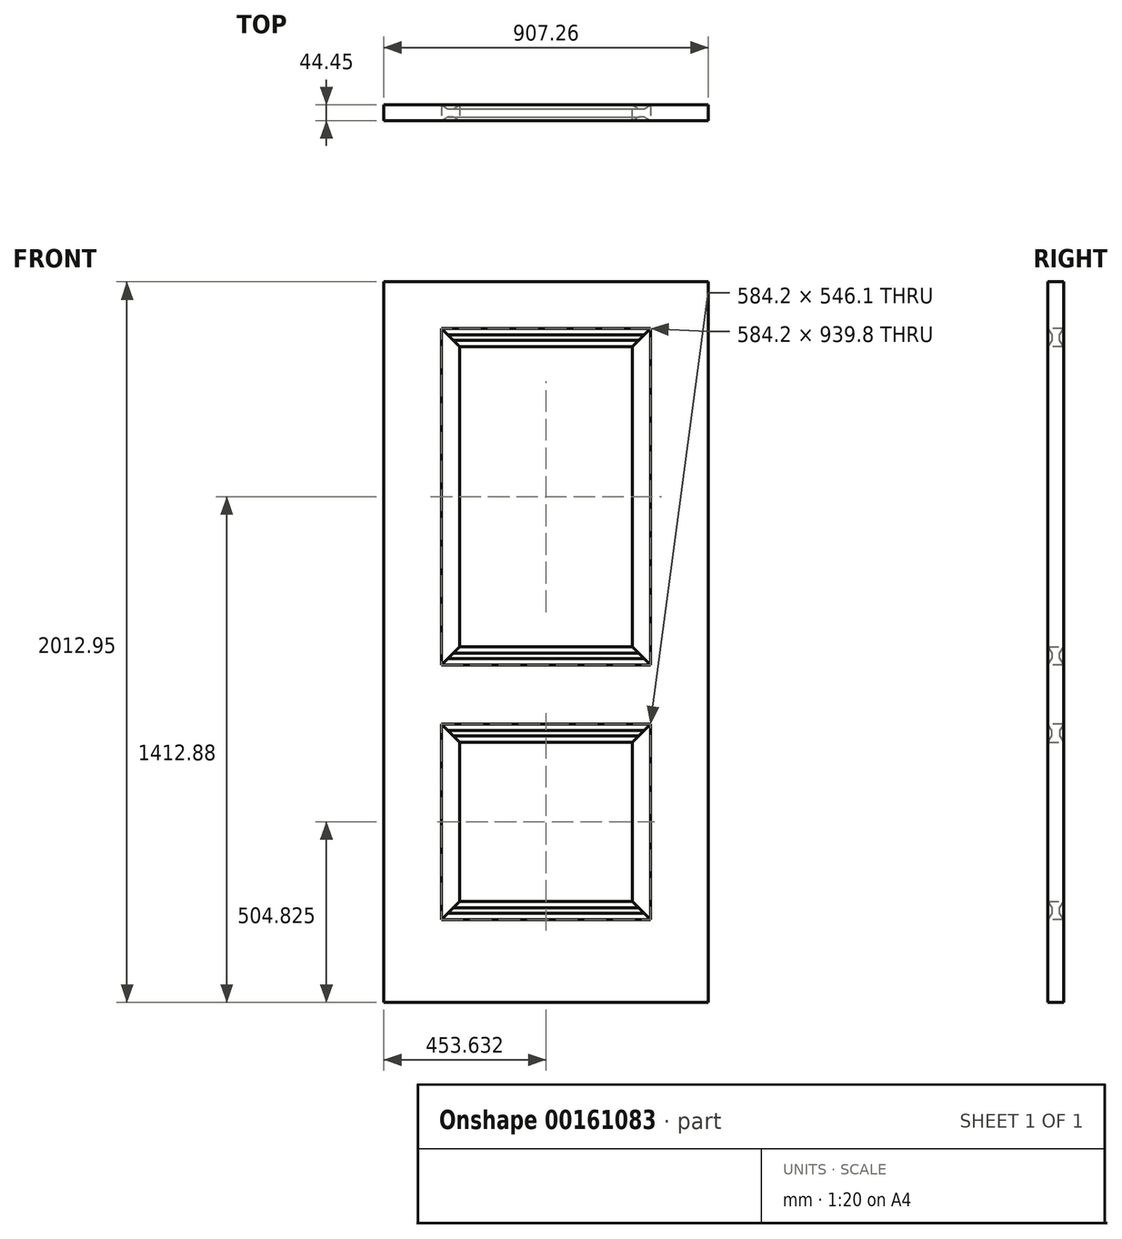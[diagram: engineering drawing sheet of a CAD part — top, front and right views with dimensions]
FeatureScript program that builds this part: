
annotation { "Feature Type Name" : "Feature", "Feature Type Description" : "" }
export const myFeature = defineFeature(function(context is Context, id is Id, definition is map)
    precondition{}
    {
        {
            var Q0;
            Q0=qCreatedBy(makeId("Top.planeOp"),FACE);
            var sketch = newSketch(context, id + "F0", { "sketchPlane" : qUnion([Q0])});
            skLineSegment(sketch, "E0.bottom", {"start": v(0, 0) * mm, "end": v(-907.26, 0) * mm});
            skLineSegment(sketch, "E0.top", {"start": v(0, 44.45) * mm, "end": v(-907.26, 44.45) * mm});
            skLineSegment(sketch, "E0.left", {"start": v(0, 0) * mm, "end": v(0, 44.45) * mm});
            skLineSegment(sketch, "E0.right", {"start": v(-907.26, 0) * mm, "end": v(-907.26, 44.45) * mm});
            skSolve(sketch);
        }
        {
            var Q0;
            Q0=qSketchRegion(id+"F0",true);
            extrude(context, id + "F1", {"entities" : qUnion([Q0]), "depth" : 2012.95 * mm});
        }
        {
            var Q0;
            Q0=qCreatedBy(makeId("Front.planeOp"),FACE);
            var sketch = newSketch(context, id + "F2", { "sketchPlane" : qUnion([Q0])});
            skLineSegment(sketch, "E1.top", {"start": v(-745.73, 942.97) * mm, "end": v(-161.53, 942.98) * mm});
            skLineSegment(sketch, "E1.left", {"start": v(-745.73, 1882.78) * mm, "end": v(-745.73, 942.97) * mm});
            skLineSegment(sketch, "E1.right", {"start": v(-161.53, 1882.78) * mm, "end": v(-161.53, 942.98) * mm});
            skLineSegment(sketch, "E2", {"start": v(-745.73, 1882.78) * mm, "end": v(-453.63, 1882.78) * mm});
            skLineSegment(sketch, "E3", {"start": v(-453.63, 1882.78) * mm, "end": v(-161.53, 1882.78) * mm});
            skPoint(sketch, "E4.0", {"position": v(-453.63, 2012.95) * mm});
            skLineSegment(sketch, "E5.bottom", {"start": v(-745.73, 777.88) * mm, "end": v(-161.53, 777.88) * mm});
            skLineSegment(sketch, "E5.top", {"start": v(-745.73, 231.78) * mm, "end": v(-161.53, 231.78) * mm});
            skLineSegment(sketch, "E5.left", {"start": v(-745.73, 777.88) * mm, "end": v(-745.73, 231.78) * mm});
            skLineSegment(sketch, "E5.right", {"start": v(-161.53, 777.88) * mm, "end": v(-161.53, 231.78) * mm});
            skSolve(sketch);
        }
        {
            var Q0;
            Q0 = qSketchRegion(id + "F2", true);
            extrude(context, id + "F3", {"entities" : qUnion([Q0]), "operationType" : NewBodyOperationType.REMOVE, "endBound" : BoundingType.THROUGH_ALL, "oppositeDirection" : true, "depth" : 25.4 * mm});
        }
        {
            var Q0;
            Q0=qCreatedBy(makeId("Top.planeOp"),FACE);
            var sketch = newSketch(context, id + "F4", { "sketchPlane" : qUnion([Q0])});
            skPoint(sketch, "E6.0", {"position": v(-161.53, 22.23) * mm});
            skPoint(sketch, "E7.0", {"position": v(-161.53, 44.45) * mm});
            skLineSegment(sketch, "E8", {"start": v(-161.53, 22.23) * mm, "end": v(-161.53, 44.45) * mm});
            skLineSegment(sketch, "E9", {"start": v(-161.53, 44.45) * mm, "end": v(-179, 33.62) * mm});
            skLineSegment(sketch, "E10", {"start": v(-179, 33.62) * mm, "end": v(-186.93, 33.62) * mm});
            skLineSegment(sketch, "E11", {"start": v(-186.93, 33.62) * mm, "end": v(-186.93, 59.2) * mm, "construction": true});
            skLineSegment(sketch, "E12", {"start": v(-161.53, 22.23) * mm, "end": v(-138.76, 22.23) * mm, "construction": true});
            skLineSegment(sketch, "E13.MirrorCS", {"start": v(-194.86, 33.62) * mm, "end": v(-186.93, 33.62) * mm});
            skLineSegment(sketch, "E14.MirrorCS", {"start": v(-212.33, 44.45) * mm, "end": v(-194.86, 33.62) * mm});
            skLineSegment(sketch, "E15.MirrorCS", {"start": v(-212.33, 22.23) * mm, "end": v(-212.33, 44.45) * mm});
            skLineSegment(sketch, "E16.MirrorCS", {"start": v(-161.53, 22.23) * mm, "end": v(-161.53, 0) * mm});
            skLineSegment(sketch, "E17.MirrorCS", {"start": v(-161.53, 0) * mm, "end": v(-179, 10.83) * mm});
            skLineSegment(sketch, "E18.MirrorCS", {"start": v(-179, 10.83) * mm, "end": v(-186.93, 10.83) * mm});
            skLineSegment(sketch, "E19.MirrorCS", {"start": v(-194.86, 10.83) * mm, "end": v(-186.93, 10.83) * mm});
            skLineSegment(sketch, "E20.MirrorCS", {"start": v(-212.33, 0) * mm, "end": v(-194.86, 10.83) * mm});
            skLineSegment(sketch, "E21.MirrorCS", {"start": v(-212.33, 22.23) * mm, "end": v(-212.33, 0) * mm});
            skPoint(sketch, "E22.0", {"position": v(-745.73, 22.23) * mm});
            skLineSegment(sketch, "E23", {"start": v(-161.53, 126.67) * mm, "end": v(-745.73, 126.67) * mm, "construction": true});
            skLineSegment(sketch, "E24", {"start": v(-453.63, 126.67) * mm, "end": v(-453.63, 173.15) * mm, "construction": true});
            skPoint(sketch, "E24.endSnap0", {"position": v(-453.63, 126.67) * mm});
            skLineSegment(sketch, "E25.MirrorCS", {"start": v(-712.4, 10.83) * mm, "end": v(-720.33, 10.83) * mm});
            skLineSegment(sketch, "E26.MirrorCS", {"start": v(-712.4, 33.62) * mm, "end": v(-720.33, 33.62) * mm});
            skLineSegment(sketch, "E27.MirrorCS", {"start": v(-728.26, 10.83) * mm, "end": v(-720.33, 10.83) * mm});
            skLineSegment(sketch, "E28.MirrorCS", {"start": v(-728.26, 33.62) * mm, "end": v(-720.33, 33.62) * mm});
            skLineSegment(sketch, "E29.MirrorCS", {"start": v(-694.93, 0) * mm, "end": v(-712.4, 10.83) * mm});
            skLineSegment(sketch, "E30.MirrorCS", {"start": v(-694.93, 44.45) * mm, "end": v(-712.4, 33.62) * mm});
            skLineSegment(sketch, "E31.MirrorCS", {"start": v(-745.73, 0) * mm, "end": v(-728.26, 10.83) * mm});
            skLineSegment(sketch, "E32.MirrorCS", {"start": v(-745.73, 22.23) * mm, "end": v(-745.73, 44.45) * mm});
            skLineSegment(sketch, "E33.MirrorCS", {"start": v(-694.93, 22.23) * mm, "end": v(-694.93, 0) * mm});
            skPoint(sketch, "E34.MirrorP", {"position": v(-745.73, 44.45) * mm});
            skLineSegment(sketch, "E35.MirrorCS", {"start": v(-745.73, 22.23) * mm, "end": v(-745.73, 0) * mm});
            skLineSegment(sketch, "E36.MirrorCS", {"start": v(-745.73, 44.45) * mm, "end": v(-728.26, 33.62) * mm});
            skLineSegment(sketch, "E37.MirrorCS", {"start": v(-694.93, 22.23) * mm, "end": v(-694.93, 44.45) * mm});
            skSolve(sketch);
        }
        {
            var Q0;
            Q0=qCreatedBy(makeId("Front.planeOp"),FACE);
            var sketch = newSketch(context, id + "F5", { "sketchPlane" : qUnion([Q0])});
            skPoint(sketch, "E38.0", {"position": v(-745.73, 1882.78) * mm});
            skPoint(sketch, "E39.0", {"position": v(-161.53, 1882.78) * mm});
            skPoint(sketch, "E40.0", {"position": v(-161.53, 942.97) * mm});
            skPoint(sketch, "E41.0", {"position": v(-745.73, 942.97) * mm});
            skPoint(sketch, "E42.0", {"position": v(-745.73, 777.88) * mm});
            skPoint(sketch, "E43.0", {"position": v(-161.53, 777.88) * mm});
            skPoint(sketch, "E44.0", {"position": v(-745.73, 231.78) * mm});
            skPoint(sketch, "E45.0", {"position": v(-161.53, 231.78) * mm});
            skLineSegment(sketch, "E46", {"start": v(-745.73, 1882.78) * mm, "end": v(-453.63, 1590.68) * mm});
            skLineSegment(sketch, "E47", {"start": v(-453.63, 1590.68) * mm, "end": v(-161.53, 1882.78) * mm});
            skLineSegment(sketch, "E48", {"start": v(-745.73, 777.88) * mm, "end": v(-453.63, 485.78) * mm});
            skLineSegment(sketch, "E49", {"start": v(-453.63, 485.77) * mm, "end": v(-161.53, 777.88) * mm});
            skLineSegment(sketch, "E50", {"start": v(-745.73, 1882.78) * mm, "end": v(-875.9, 2012.95) * mm});
            skLineSegment(sketch, "E51", {"start": v(-875.9, 2012.95) * mm, "end": v(-31.35, 2012.95) * mm});
            skLineSegment(sketch, "E52", {"start": v(-31.35, 2012.95) * mm, "end": v(-161.53, 1882.78) * mm});
            skLineSegment(sketch, "E53", {"start": v(-745.73, 777.88) * mm, "end": v(-1980.8, 2012.95) * mm});
            skLineSegment(sketch, "E54", {"start": v(-1980.8, 2012.95) * mm, "end": v(1073.55, 2012.95) * mm});
            skLineSegment(sketch, "E55", {"start": v(1073.55, 2012.95) * mm, "end": v(-161.53, 777.88) * mm});
            skLineSegment(sketch, "E56", {"start": v(-745.73, 942.97) * mm, "end": v(-453.63, 1235.07) * mm});
            skLineSegment(sketch, "E57", {"start": v(-453.63, 1235.07) * mm, "end": v(-161.53, 942.97) * mm});
            skLineSegment(sketch, "E58", {"start": v(-745.73, 231.77) * mm, "end": v(-453.63, 523.88) * mm});
            skLineSegment(sketch, "E59", {"start": v(-453.63, 523.88) * mm, "end": v(-161.53, 231.78) * mm});
            skLineSegment(sketch, "E60", {"start": v(-745.73, 942.97) * mm, "end": v(-1688.7, 0) * mm});
            skLineSegment(sketch, "E61", {"start": v(-1688.7, 0) * mm, "end": v(781.45, 0) * mm});
            skLineSegment(sketch, "E62", {"start": v(781.45, 0) * mm, "end": v(-161.53, 942.98) * mm});
            skLineSegment(sketch, "E63", {"start": v(-161.53, 231.78) * mm, "end": v(70.25, 0) * mm});
            skLineSegment(sketch, "E64", {"start": v(70.25, 0) * mm, "end": v(-977.5, 0) * mm});
            skLineSegment(sketch, "E65", {"start": v(-977.5, 0) * mm, "end": v(-745.73, 231.78) * mm});
            skSolve(sketch);
        }
        {
            var Q0;
            Q0=makeQuery(id+"F3.boolean.opBoolean","COPY",FACE,{"derivedFrom":makeQuery(id+"F3.opExtrude","SWEPT_FACE",FACE,{"disambiguationData":[OSD([sQuery(id+"F2.wireOp",EDGE,"E2"),sQuery(id+"F2.wireOp",EDGE,"E3")])]})});
            var sketch = newSketch(context, id + "F6", { "sketchPlane" : qUnion([Q0])});
            skLineSegment(sketch, "E66.2", {"start": v(-694.93, 0) * mm, "end": v(-712.4, -10.83) * mm});
            skLineSegment(sketch, "E66.4", {"start": v(-212.33, -44.45) * mm, "end": v(-194.86, -33.62) * mm});
            skLineSegment(sketch, "E66.5", {"start": v(-694.93, -22.23) * mm, "end": v(-694.93, 0) * mm});
            skLineSegment(sketch, "E66.6", {"start": v(-212.33, -22.23) * mm, "end": v(-212.33, -44.45) * mm});
            skLineSegment(sketch, "E66.7", {"start": v(-694.93, -44.45) * mm, "end": v(-712.4, -33.62) * mm});
            skLineSegment(sketch, "E66.8", {"start": v(-212.33, 0) * mm, "end": v(-194.86, -10.83) * mm});
            skLineSegment(sketch, "E66.9", {"start": v(-212.33, -22.23) * mm, "end": v(-212.33, 0) * mm});
            skLineSegment(sketch, "E66.10", {"start": v(-694.93, -22.23) * mm, "end": v(-694.93, -44.45) * mm});
            skLineSegment(sketch, "E66.11", {"start": v(-161.53, -44.45) * mm, "end": v(-179, -33.62) * mm});
            skLineSegment(sketch, "E66.12", {"start": v(-712.4, -33.62) * mm, "end": v(-720.33, -33.62) * mm});
            skLineSegment(sketch, "E66.14", {"start": v(-194.86, -33.62) * mm, "end": v(-186.93, -33.62) * mm});
            skLineSegment(sketch, "E66.15", {"start": v(-745.73, -44.45) * mm, "end": v(-728.26, -33.62) * mm});
            skLineSegment(sketch, "E66.16", {"start": v(-161.53, -22.23) * mm, "end": v(-161.53, 0) * mm});
            skLineSegment(sketch, "E66.17", {"start": v(-161.53, 0) * mm, "end": v(-179, -10.83) * mm});
            skLineSegment(sketch, "E66.18", {"start": v(-179, -10.83) * mm, "end": v(-186.93, -10.83) * mm});
            skLineSegment(sketch, "E66.19", {"start": v(-194.86, -10.83) * mm, "end": v(-186.93, -10.83) * mm});
            skLineSegment(sketch, "E66.20", {"start": v(-745.73, 0) * mm, "end": v(-728.26, -10.83) * mm});
            skLineSegment(sketch, "E66.21", {"start": v(-745.73, -22.23) * mm, "end": v(-745.73, -44.45) * mm});
            skLineSegment(sketch, "E66.22", {"start": v(-728.26, -10.83) * mm, "end": v(-720.33, -10.83) * mm});
            skLineSegment(sketch, "E66.23", {"start": v(-745.73, -22.23) * mm, "end": v(-745.73, 0) * mm});
            skLineSegment(sketch, "E66.24", {"start": v(-712.4, -10.83) * mm, "end": v(-720.33, -10.83) * mm});
            skLineSegment(sketch, "E66.25", {"start": v(-161.53, -22.23) * mm, "end": v(-161.53, -44.45) * mm});
            skLineSegment(sketch, "E66.26", {"start": v(-179, -33.62) * mm, "end": v(-186.93, -33.62) * mm});
            skLineSegment(sketch, "E66.27", {"start": v(-728.26, -33.62) * mm, "end": v(-720.33, -33.62) * mm});
            skSolve(sketch);
        }
        {
            var Q0;
            Q0=makeQuery(id+"F3.boolean.opBoolean","COPY",FACE,{"derivedFrom":makeQuery(id+"F3.opExtrude","SWEPT_FACE",FACE,{"disambiguationData":[OSD([sQuery(id+"F2.wireOp",EDGE,"E5.top")])]})});
            var sketch = newSketch(context, id + "F7", { "sketchPlane" : qUnion([Q0])});
            skLineSegment(sketch, "E67.0", {"start": v(-745.73, 0) * mm, "end": v(-728.26, 10.83) * mm});
            skLineSegment(sketch, "E67.1", {"start": v(-694.93, 0) * mm, "end": v(-712.4, 10.83) * mm});
            skLineSegment(sketch, "E67.2", {"start": v(-745.73, 22.23) * mm, "end": v(-745.73, 44.45) * mm});
            skLineSegment(sketch, "E67.3", {"start": v(-728.26, 10.83) * mm, "end": v(-720.33, 10.83) * mm});
            skLineSegment(sketch, "E67.4", {"start": v(-745.73, 22.23) * mm, "end": v(-745.73, 0) * mm});
            skLineSegment(sketch, "E67.5", {"start": v(-694.93, 22.23) * mm, "end": v(-694.93, 44.45) * mm});
            skLineSegment(sketch, "E67.6", {"start": v(-712.4, 10.83) * mm, "end": v(-720.33, 10.83) * mm});
            skLineSegment(sketch, "E67.7", {"start": v(-712.4, 33.62) * mm, "end": v(-720.33, 33.62) * mm});
            skLineSegment(sketch, "E67.8", {"start": v(-745.73, 44.45) * mm, "end": v(-728.26, 33.62) * mm});
            skLineSegment(sketch, "E67.9", {"start": v(-694.93, 22.23) * mm, "end": v(-694.93, 0) * mm});
            skLineSegment(sketch, "E67.10", {"start": v(-694.93, 44.45) * mm, "end": v(-712.4, 33.62) * mm});
            skLineSegment(sketch, "E67.11", {"start": v(-728.26, 33.62) * mm, "end": v(-720.33, 33.62) * mm});
            skLineSegment(sketch, "E68.0", {"start": v(-212.33, 22.23) * mm, "end": v(-212.33, 0) * mm});
            skLineSegment(sketch, "E68.1", {"start": v(-161.53, 22.23) * mm, "end": v(-161.53, 44.45) * mm});
            skLineSegment(sketch, "E68.2", {"start": v(-161.53, 44.45) * mm, "end": v(-179, 33.62) * mm});
            skLineSegment(sketch, "E68.3", {"start": v(-179, 33.62) * mm, "end": v(-186.93, 33.62) * mm});
            skLineSegment(sketch, "E68.4", {"start": v(-194.86, 33.62) * mm, "end": v(-186.93, 33.62) * mm});
            skLineSegment(sketch, "E68.5", {"start": v(-212.33, 44.45) * mm, "end": v(-194.86, 33.62) * mm});
            skLineSegment(sketch, "E68.6", {"start": v(-212.33, 22.23) * mm, "end": v(-212.33, 44.45) * mm});
            skLineSegment(sketch, "E68.7", {"start": v(-161.53, 22.23) * mm, "end": v(-161.53, 0) * mm});
            skLineSegment(sketch, "E68.8", {"start": v(-161.53, 0) * mm, "end": v(-179, 10.83) * mm});
            skLineSegment(sketch, "E68.9", {"start": v(-179, 10.83) * mm, "end": v(-186.93, 10.83) * mm});
            skLineSegment(sketch, "E68.10", {"start": v(-194.86, 10.83) * mm, "end": v(-186.93, 10.83) * mm});
            skLineSegment(sketch, "E68.11", {"start": v(-212.33, 0) * mm, "end": v(-194.86, 10.83) * mm});
            skSolve(sketch);
        }
        {
            var Q0;
            Q0 = qSketchRegion(id + "F6", true);
            var Q1;
            Q1=makeQuery(id+"F3.boolean.opBoolean","COPY",FACE,{"derivedFrom":makeQuery(id+"F3.opExtrude","SWEPT_FACE",FACE,{"disambiguationData":[OSD([sQuery(id+"F2.wireOp",EDGE,"E1.top")])]})});
            extrude(context, id + "F8", {"entities" : qUnion([Q0]), "operationType" : NewBodyOperationType.ADD, "endBound" : BoundingType.UP_TO_SURFACE, "endBoundEntityFace" : qUnion([Q1]), "depth" : 307.34 * mm});
        }
        {
            var Q0;
            Q0 = qSketchRegion(id + "F7", true);
            var Q1;
            Q1=makeQuery(id+"F3.boolean.opBoolean","COPY",FACE,{"derivedFrom":makeQuery(id+"F3.opExtrude","SWEPT_FACE",FACE,{"disambiguationData":[OSD([sQuery(id+"F2.wireOp",EDGE,"E5.bottom")])]})});
            extrude(context, id + "F9", {"entities" : qUnion([Q0]), "operationType" : NewBodyOperationType.ADD, "endBound" : BoundingType.UP_TO_SURFACE, "endBoundEntityFace" : qUnion([Q1]), "depth" : 25.4 * mm});
        }
        {
            var Q0;
            Q0=qCreatedBy(makeId("Front.planeOp"),FACE);
            var sketch = newSketch(context, id + "F10", { "sketchPlane" : qUnion([Q0])});
            skLineSegment(sketch, "E69.0", {"start": v(-453.63, 1590.68) * mm, "end": v(-161.53, 1882.78) * mm});
            skLineSegment(sketch, "E70.0", {"start": v(-745.73, 1882.78) * mm, "end": v(-453.63, 1590.68) * mm});
            skLineSegment(sketch, "E71.0", {"start": v(-212.33, 1882.78) * mm, "end": v(-161.53, 1882.78) * mm});
            skLineSegment(sketch, "E72.0", {"start": v(-694.93, 1882.78) * mm, "end": v(-212.33, 1882.78) * mm});
            skLineSegment(sketch, "E73.0", {"start": v(-745.73, 1882.78) * mm, "end": v(-694.93, 1882.78) * mm});
            skLineSegment(sketch, "E74.0", {"start": v(-453.63, 1235.07) * mm, "end": v(-161.53, 942.97) * mm});
            skLineSegment(sketch, "E75.0", {"start": v(-745.73, 942.97) * mm, "end": v(-453.63, 1235.07) * mm});
            skLineSegment(sketch, "E76.0", {"start": v(-694.93, 942.97) * mm, "end": v(-212.33, 942.98) * mm});
            skLineSegment(sketch, "E77.0", {"start": v(-212.33, 942.98) * mm, "end": v(-161.53, 942.98) * mm});
            skLineSegment(sketch, "E78.0", {"start": v(-745.73, 942.97) * mm, "end": v(-694.93, 942.97) * mm});
            skLineSegment(sketch, "E79.0", {"start": v(-212.33, 777.88) * mm, "end": v(-161.53, 777.88) * mm});
            skLineSegment(sketch, "E80.0", {"start": v(-694.93, 777.88) * mm, "end": v(-212.33, 777.88) * mm});
            skLineSegment(sketch, "E81.0", {"start": v(-745.73, 777.88) * mm, "end": v(-694.93, 777.88) * mm});
            skLineSegment(sketch, "E82.0", {"start": v(-453.63, 485.78) * mm, "end": v(-161.53, 777.88) * mm});
            skLineSegment(sketch, "E83.0", {"start": v(-745.73, 777.88) * mm, "end": v(-453.63, 485.78) * mm});
            skLineSegment(sketch, "E84.0", {"start": v(-694.93, 231.78) * mm, "end": v(-212.33, 231.78) * mm});
            skLineSegment(sketch, "E85.0", {"start": v(-212.33, 231.78) * mm, "end": v(-161.53, 231.78) * mm});
            skLineSegment(sketch, "E86.0", {"start": v(-745.73, 231.78) * mm, "end": v(-694.93, 231.78) * mm});
            skLineSegment(sketch, "E87.0", {"start": v(-745.73, 231.77) * mm, "end": v(-453.63, 523.88) * mm});
            skLineSegment(sketch, "E88.0", {"start": v(-453.63, 523.88) * mm, "end": v(-161.53, 231.78) * mm});
            skSolve(sketch);
        }
        {
            var Q0;
            Q0 = qSketchRegion(id + "F10", true);
            extrude(context, id + "F11", {"entities" : qUnion([Q0]), "operationType" : NewBodyOperationType.REMOVE, "endBound" : BoundingType.THROUGH_ALL, "oppositeDirection" : true, "depth" : 25.4 * mm});
        }
        {
            var Q0;
            Q0=qCreatedBy(makeId("Right.planeOp"),FACE);
            var sketch = newSketch(context, id + "F12", { "sketchPlane" : qUnion([Q0])});
            skLineSegment(sketch, "E89.0.0", {"start": v(0, 1882.78) * mm, "end": v(44.45, 1882.78) * mm});
            skLineSegment(sketch, "E89.0.1", {"start": v(44.45, 1882.77) * mm, "end": v(33.62, 1865.3) * mm});
            skLineSegment(sketch, "E89.0.2", {"start": v(33.62, 1865.3) * mm, "end": v(33.62, 1849.44) * mm});
            skLineSegment(sketch, "E89.0.3", {"start": v(33.62, 1849.44) * mm, "end": v(44.45, 1831.97) * mm});
            skLineSegment(sketch, "E89.0.4", {"start": v(44.45, 1831.97) * mm, "end": v(0, 1831.97) * mm});
            skLineSegment(sketch, "E89.0.5", {"start": v(0, 1831.97) * mm, "end": v(10.83, 1849.44) * mm});
            skLineSegment(sketch, "E89.0.6", {"start": v(10.83, 1849.44) * mm, "end": v(10.83, 1865.3) * mm});
            skLineSegment(sketch, "E89.0.7", {"start": v(10.83, 1865.3) * mm, "end": v(0, 1882.78) * mm});
            skLineSegment(sketch, "E90.0.0", {"start": v(0, 942.98) * mm, "end": v(10.83, 960.44) * mm});
            skLineSegment(sketch, "E90.0.1", {"start": v(10.83, 960.44) * mm, "end": v(10.83, 976.3) * mm});
            skLineSegment(sketch, "E90.0.2", {"start": v(10.83, 976.3) * mm, "end": v(0, 993.78) * mm});
            skLineSegment(sketch, "E90.0.3", {"start": v(0, 993.78) * mm, "end": v(44.45, 993.78) * mm});
            skLineSegment(sketch, "E90.0.4", {"start": v(44.45, 993.77) * mm, "end": v(33.62, 976.3) * mm});
            skLineSegment(sketch, "E90.0.5", {"start": v(33.62, 976.3) * mm, "end": v(33.62, 960.44) * mm});
            skLineSegment(sketch, "E90.0.6", {"start": v(33.62, 960.44) * mm, "end": v(44.45, 942.98) * mm});
            skLineSegment(sketch, "E90.0.7", {"start": v(44.45, 942.97) * mm, "end": v(0, 942.97) * mm});
            skLineSegment(sketch, "E91.0.0", {"start": v(33.62, 760.4) * mm, "end": v(33.62, 744.54) * mm});
            skLineSegment(sketch, "E91.0.1", {"start": v(33.62, 744.54) * mm, "end": v(44.45, 727.07) * mm});
            skLineSegment(sketch, "E91.0.2", {"start": v(44.45, 727.07) * mm, "end": v(0, 727.07) * mm});
            skLineSegment(sketch, "E91.0.3", {"start": v(0, 727.08) * mm, "end": v(10.83, 744.54) * mm});
            skLineSegment(sketch, "E91.0.4", {"start": v(10.83, 744.54) * mm, "end": v(10.83, 760.4) * mm});
            skLineSegment(sketch, "E91.0.5", {"start": v(10.83, 760.4) * mm, "end": v(0, 777.88) * mm});
            skLineSegment(sketch, "E91.0.6", {"start": v(0, 777.88) * mm, "end": v(44.45, 777.88) * mm});
            skLineSegment(sketch, "E91.0.7", {"start": v(44.45, 777.87) * mm, "end": v(33.62, 760.4) * mm});
            skLineSegment(sketch, "E92.0.0", {"start": v(33.62, 249.24) * mm, "end": v(44.45, 231.77) * mm});
            skLineSegment(sketch, "E92.0.1", {"start": v(44.45, 231.78) * mm, "end": v(0, 231.78) * mm});
            skLineSegment(sketch, "E92.0.2", {"start": v(0, 231.78) * mm, "end": v(10.83, 249.24) * mm});
            skLineSegment(sketch, "E92.0.3", {"start": v(10.83, 249.24) * mm, "end": v(10.83, 265.1) * mm});
            skLineSegment(sketch, "E92.0.4", {"start": v(10.83, 265.1) * mm, "end": v(0, 282.58) * mm});
            skLineSegment(sketch, "E92.0.5", {"start": v(0, 282.58) * mm, "end": v(44.45, 282.58) * mm});
            skLineSegment(sketch, "E92.0.6", {"start": v(44.45, 282.57) * mm, "end": v(33.62, 265.1) * mm});
            skLineSegment(sketch, "E92.0.7", {"start": v(33.62, 265.1) * mm, "end": v(33.62, 249.24) * mm});
            skSolve(sketch);
        }
        {
            var Q0;
            Q0 = qSketchRegion(id + "F12", true);
            var Q1;
            Q1=makeQuery(id+"F1.opExtrude","SWEPT_FACE",FACE,{"disambiguationData":[OSD([sQuery(id+"F0.wireOp",EDGE,"E0.right")])]});
            extrude(context, id + "F13", {"entities" : qUnion([Q0]), "endBound" : BoundingType.UP_TO_SURFACE, "oppositeDirection" : true, "endBoundEntityFace" : qUnion([Q1]), "depth" : 25.4 * mm});
        }
        {
            var Q0;
            Q0=qCreatedBy(makeId("Front.planeOp"),FACE);
            var sketch = newSketch(context, id + "F14", { "sketchPlane" : qUnion([Q0])});
            skLineSegment(sketch, "E93.0", {"start": v(-745.73, 231.77) * mm, "end": v(-453.63, 523.88) * mm});
            skLineSegment(sketch, "E94.0", {"start": v(-745.73, 777.88) * mm, "end": v(-453.63, 485.78) * mm});
            skLineSegment(sketch, "E95.0", {"start": v(-453.63, 523.88) * mm, "end": v(-161.53, 231.78) * mm});
            skLineSegment(sketch, "E96.0", {"start": v(-453.63, 485.78) * mm, "end": v(-161.53, 777.88) * mm});
            skLineSegment(sketch, "E97", {"start": v(-161.53, 777.88) * mm, "end": v(-161.53, 231.78) * mm});
            skLineSegment(sketch, "E98", {"start": v(-745.73, 777.88) * mm, "end": v(-745.73, 231.77) * mm});
            skLineSegment(sketch, "E99.0", {"start": v(-453.63, 1590.68) * mm, "end": v(-161.53, 1882.78) * mm});
            skLineSegment(sketch, "E100.0", {"start": v(-745.73, 1882.78) * mm, "end": v(-453.63, 1590.68) * mm});
            skLineSegment(sketch, "E101.0", {"start": v(-745.73, 942.97) * mm, "end": v(-453.63, 1235.07) * mm});
            skLineSegment(sketch, "E102.0", {"start": v(-453.63, 1235.07) * mm, "end": v(-161.53, 942.97) * mm});
            skLineSegment(sketch, "E103", {"start": v(-161.53, 1882.78) * mm, "end": v(-161.53, 942.97) * mm});
            skLineSegment(sketch, "E104", {"start": v(-745.73, 942.97) * mm, "end": v(-745.73, 1882.78) * mm});
            skSolve(sketch);
        }
        {
            var Q0;
            Q0 = qSketchRegion(id + "F14", true);
            extrude(context, id + "F15", {"entities" : qUnion([Q0]), "operationType" : NewBodyOperationType.REMOVE, "endBound" : BoundingType.THROUGH_ALL, "oppositeDirection" : true, "depth" : 25.4 * mm});
        }
        {
            var Q0;
            Q0=makeQuery(id+"F1.opExtrude","SWEPT_BODY",BODY,{"disambiguationData":[OSD([sQuery(id+"F0.wireOp",EDGE,"E0.bottom"),sQuery(id+"F0.wireOp",EDGE,"E0.top"),sQuery(id+"F0.wireOp",EDGE,"E0.left"),sQuery(id+"F0.wireOp",EDGE,"E0.right")])]});
            var Q1;
            Q1=makeQuery(id+"F15.boolean.opBoolean","SPLIT",BODY,{"disambiguationData":[OD(0.0)],"derivedFrom":makeQuery(id+"F13.opExtrude","SWEPT_BODY",BODY,{"disambiguationData":[OSD([sQuery(id+"F12.wireOp",EDGE,"E89.0.0"),sQuery(id+"F12.wireOp",EDGE,"E89.0.1"),sQuery(id+"F12.wireOp",EDGE,"E89.0.2"),sQuery(id+"F12.wireOp",EDGE,"E89.0.3"),sQuery(id+"F12.wireOp",EDGE,"E89.0.4"),sQuery(id+"F12.wireOp",EDGE,"E89.0.5"),sQuery(id+"F12.wireOp",EDGE,"E89.0.6"),sQuery(id+"F12.wireOp",EDGE,"E89.0.7")])]})});
            var Q2;
            Q2=makeQuery(id+"F15.boolean.opBoolean","SPLIT",BODY,{"disambiguationData":[OD(1.0)],"derivedFrom":makeQuery(id+"F13.opExtrude","SWEPT_BODY",BODY,{"disambiguationData":[OSD([sQuery(id+"F12.wireOp",EDGE,"E89.0.0"),sQuery(id+"F12.wireOp",EDGE,"E89.0.1"),sQuery(id+"F12.wireOp",EDGE,"E89.0.2"),sQuery(id+"F12.wireOp",EDGE,"E89.0.3"),sQuery(id+"F12.wireOp",EDGE,"E89.0.4"),sQuery(id+"F12.wireOp",EDGE,"E89.0.5"),sQuery(id+"F12.wireOp",EDGE,"E89.0.6"),sQuery(id+"F12.wireOp",EDGE,"E89.0.7")])]})});
            var Q3;
            Q3=makeQuery(id+"F15.boolean.opBoolean","SPLIT",BODY,{"disambiguationData":[OD(2.0)],"derivedFrom":makeQuery(id+"F13.opExtrude","SWEPT_BODY",BODY,{"disambiguationData":[OSD([sQuery(id+"F12.wireOp",EDGE,"E89.0.0"),sQuery(id+"F12.wireOp",EDGE,"E89.0.1"),sQuery(id+"F12.wireOp",EDGE,"E89.0.2"),sQuery(id+"F12.wireOp",EDGE,"E89.0.3"),sQuery(id+"F12.wireOp",EDGE,"E89.0.4"),sQuery(id+"F12.wireOp",EDGE,"E89.0.5"),sQuery(id+"F12.wireOp",EDGE,"E89.0.6"),sQuery(id+"F12.wireOp",EDGE,"E89.0.7")])]})});
            var Q4;
            Q4=makeQuery(id+"F15.boolean.opBoolean","SPLIT",BODY,{"disambiguationData":[OD(0.0)],"derivedFrom":makeQuery(id+"F13.opExtrude","SWEPT_BODY",BODY,{"disambiguationData":[OSD([sQuery(id+"F12.wireOp",EDGE,"E90.0.0"),sQuery(id+"F12.wireOp",EDGE,"E90.0.1"),sQuery(id+"F12.wireOp",EDGE,"E90.0.2"),sQuery(id+"F12.wireOp",EDGE,"E90.0.3"),sQuery(id+"F12.wireOp",EDGE,"E90.0.4"),sQuery(id+"F12.wireOp",EDGE,"E90.0.5"),sQuery(id+"F12.wireOp",EDGE,"E90.0.6"),sQuery(id+"F12.wireOp",EDGE,"E90.0.7")])]})});
            var Q5;
            Q5=makeQuery(id+"F15.boolean.opBoolean","SPLIT",BODY,{"disambiguationData":[OD(1.0)],"derivedFrom":makeQuery(id+"F13.opExtrude","SWEPT_BODY",BODY,{"disambiguationData":[OSD([sQuery(id+"F12.wireOp",EDGE,"E90.0.0"),sQuery(id+"F12.wireOp",EDGE,"E90.0.1"),sQuery(id+"F12.wireOp",EDGE,"E90.0.2"),sQuery(id+"F12.wireOp",EDGE,"E90.0.3"),sQuery(id+"F12.wireOp",EDGE,"E90.0.4"),sQuery(id+"F12.wireOp",EDGE,"E90.0.5"),sQuery(id+"F12.wireOp",EDGE,"E90.0.6"),sQuery(id+"F12.wireOp",EDGE,"E90.0.7")])]})});
            var Q6;
            Q6=makeQuery(id+"F15.boolean.opBoolean","SPLIT",BODY,{"disambiguationData":[OD(2.0)],"derivedFrom":makeQuery(id+"F13.opExtrude","SWEPT_BODY",BODY,{"disambiguationData":[OSD([sQuery(id+"F12.wireOp",EDGE,"E90.0.0"),sQuery(id+"F12.wireOp",EDGE,"E90.0.1"),sQuery(id+"F12.wireOp",EDGE,"E90.0.2"),sQuery(id+"F12.wireOp",EDGE,"E90.0.3"),sQuery(id+"F12.wireOp",EDGE,"E90.0.4"),sQuery(id+"F12.wireOp",EDGE,"E90.0.5"),sQuery(id+"F12.wireOp",EDGE,"E90.0.6"),sQuery(id+"F12.wireOp",EDGE,"E90.0.7")])]})});
            var Q7;
            Q7=makeQuery(id+"F15.boolean.opBoolean","SPLIT",BODY,{"disambiguationData":[OD(0.0)],"derivedFrom":makeQuery(id+"F13.opExtrude","SWEPT_BODY",BODY,{"disambiguationData":[OSD([sQuery(id+"F12.wireOp",EDGE,"E91.0.0"),sQuery(id+"F12.wireOp",EDGE,"E91.0.1"),sQuery(id+"F12.wireOp",EDGE,"E91.0.2"),sQuery(id+"F12.wireOp",EDGE,"E91.0.3"),sQuery(id+"F12.wireOp",EDGE,"E91.0.4"),sQuery(id+"F12.wireOp",EDGE,"E91.0.5"),sQuery(id+"F12.wireOp",EDGE,"E91.0.6"),sQuery(id+"F12.wireOp",EDGE,"E91.0.7")])]})});
            var Q8;
            Q8=makeQuery(id+"F15.boolean.opBoolean","SPLIT",BODY,{"disambiguationData":[OD(1.0)],"derivedFrom":makeQuery(id+"F13.opExtrude","SWEPT_BODY",BODY,{"disambiguationData":[OSD([sQuery(id+"F12.wireOp",EDGE,"E91.0.0"),sQuery(id+"F12.wireOp",EDGE,"E91.0.1"),sQuery(id+"F12.wireOp",EDGE,"E91.0.2"),sQuery(id+"F12.wireOp",EDGE,"E91.0.3"),sQuery(id+"F12.wireOp",EDGE,"E91.0.4"),sQuery(id+"F12.wireOp",EDGE,"E91.0.5"),sQuery(id+"F12.wireOp",EDGE,"E91.0.6"),sQuery(id+"F12.wireOp",EDGE,"E91.0.7")])]})});
            var Q9;
            Q9=makeQuery(id+"F15.boolean.opBoolean","SPLIT",BODY,{"disambiguationData":[OD(2.0)],"derivedFrom":makeQuery(id+"F13.opExtrude","SWEPT_BODY",BODY,{"disambiguationData":[OSD([sQuery(id+"F12.wireOp",EDGE,"E91.0.0"),sQuery(id+"F12.wireOp",EDGE,"E91.0.1"),sQuery(id+"F12.wireOp",EDGE,"E91.0.2"),sQuery(id+"F12.wireOp",EDGE,"E91.0.3"),sQuery(id+"F12.wireOp",EDGE,"E91.0.4"),sQuery(id+"F12.wireOp",EDGE,"E91.0.5"),sQuery(id+"F12.wireOp",EDGE,"E91.0.6"),sQuery(id+"F12.wireOp",EDGE,"E91.0.7")])]})});
            var Q10;
            Q10=makeQuery(id+"F15.boolean.opBoolean","SPLIT",BODY,{"disambiguationData":[OD(0.0)],"derivedFrom":makeQuery(id+"F13.opExtrude","SWEPT_BODY",BODY,{"disambiguationData":[OSD([sQuery(id+"F12.wireOp",EDGE,"E92.0.0"),sQuery(id+"F12.wireOp",EDGE,"E92.0.1"),sQuery(id+"F12.wireOp",EDGE,"E92.0.2"),sQuery(id+"F12.wireOp",EDGE,"E92.0.3"),sQuery(id+"F12.wireOp",EDGE,"E92.0.4"),sQuery(id+"F12.wireOp",EDGE,"E92.0.5"),sQuery(id+"F12.wireOp",EDGE,"E92.0.6"),sQuery(id+"F12.wireOp",EDGE,"E92.0.7")])]})});
            var Q11;
            Q11=makeQuery(id+"F15.boolean.opBoolean","SPLIT",BODY,{"disambiguationData":[OD(1.0)],"derivedFrom":makeQuery(id+"F13.opExtrude","SWEPT_BODY",BODY,{"disambiguationData":[OSD([sQuery(id+"F12.wireOp",EDGE,"E92.0.0"),sQuery(id+"F12.wireOp",EDGE,"E92.0.1"),sQuery(id+"F12.wireOp",EDGE,"E92.0.2"),sQuery(id+"F12.wireOp",EDGE,"E92.0.3"),sQuery(id+"F12.wireOp",EDGE,"E92.0.4"),sQuery(id+"F12.wireOp",EDGE,"E92.0.5"),sQuery(id+"F12.wireOp",EDGE,"E92.0.6"),sQuery(id+"F12.wireOp",EDGE,"E92.0.7")])]})});
            var Q12;
            Q12=makeQuery(id+"F15.boolean.opBoolean","SPLIT",BODY,{"disambiguationData":[OD(2.0)],"derivedFrom":makeQuery(id+"F13.opExtrude","SWEPT_BODY",BODY,{"disambiguationData":[OSD([sQuery(id+"F12.wireOp",EDGE,"E92.0.0"),sQuery(id+"F12.wireOp",EDGE,"E92.0.1"),sQuery(id+"F12.wireOp",EDGE,"E92.0.2"),sQuery(id+"F12.wireOp",EDGE,"E92.0.3"),sQuery(id+"F12.wireOp",EDGE,"E92.0.4"),sQuery(id+"F12.wireOp",EDGE,"E92.0.5"),sQuery(id+"F12.wireOp",EDGE,"E92.0.6"),sQuery(id+"F12.wireOp",EDGE,"E92.0.7")])]})});
            booleanBodies(context, id + "F16", {"operationType" : BooleanOperationType.UNION, "tools" : qUnion([Q0, Q1, Q2, Q3, Q4, Q5, Q6, Q7, Q8, Q9, Q10, Q11, Q12])});
        }
        {
            var Q0;
            Q0=makeQuery(id+"F15.boolean.opBoolean","SPLIT",FACE,{"disambiguationData":[TD([makeQuery(id+"F15.opExtrude","SWEPT_FACE",FACE,{"disambiguationData":[OSD([sQuery(id+"F14.wireOp",EDGE,"E101.0")])]})])],"derivedFrom":makeQuery(id+"F13.opExtrude","SWEPT_FACE",FACE,{"disambiguationData":[OSD([sQuery(id+"F12.wireOp",EDGE,"E90.0.3")])]})});
            var sketch = newSketch(context, id + "F17", { "sketchPlane" : qUnion([Q0])});
            skLineSegment(sketch, "E105.0.0", {"start": v(-212.33, 44.45) * mm, "end": v(-694.93, 44.45) * mm});
            skLineSegment(sketch, "E105.0.1", {"start": v(-694.93, 44.45) * mm, "end": v(-694.93, 0) * mm});
            skLineSegment(sketch, "E105.0.2", {"start": v(-694.93, 0) * mm, "end": v(-212.33, 0) * mm});
            skLineSegment(sketch, "E105.0.3", {"start": v(-212.33, 0) * mm, "end": v(-212.33, 44.45) * mm});
            skSolve(sketch);
        }
        {
            var Q0;
            Q0 = qSketchRegion(id + "F17", true);
            var Q1;
            Q1=makeQuery(id+"F15.boolean.opBoolean","SPLIT",FACE,{"disambiguationData":[TD([makeQuery(id+"F15.opExtrude","SWEPT_FACE",FACE,{"disambiguationData":[OSD([sQuery(id+"F14.wireOp",EDGE,"E99.0")])]})])],"derivedFrom":makeQuery(id+"F13.opExtrude","SWEPT_FACE",FACE,{"disambiguationData":[OSD([sQuery(id+"F12.wireOp",EDGE,"E89.0.4")])]})});
            extrude(context, id + "F18", {"entities" : qUnion([Q0]), "operationType" : NewBodyOperationType.ADD, "endBound" : BoundingType.UP_TO_SURFACE, "endBoundEntityFace" : qUnion([Q1]), "depth" : 25.4 * mm});
        }
        {
            var Q0;
            {var subQ0=sQuery(id+"F14.wireOp",EDGE,"E93.0");Q0=makeQuery(id+"F15.boolean.opBoolean","SPLIT",FACE,{"disambiguationData":[TD([makeQuery(id+"F15.opExtrude","SWEPT_FACE",FACE,{"disambiguationData":[OSD([subQ0]),TDD([makeQuery(id+"F14.imprint","IMPRINT",EDGE,{"disambiguationData":[TD([[makeQuery(id+"F14.imprint","INTERSECT",VERTEX,{"derivedFrom":[subQ0,sQuery(id+"F14.wireOp",EDGE,"E98")]}),-1.0]])],"derivedFrom":subQ0})])]})])],"derivedFrom":makeQuery(id+"F13.opExtrude","SWEPT_FACE",FACE,{"disambiguationData":[OSD([sQuery(id+"F12.wireOp",EDGE,"E92.0.5")])]})});}
            var sketch = newSketch(context, id + "F19", { "sketchPlane" : qUnion([Q0])});
            skLineSegment(sketch, "E106.0.0", {"start": v(-694.93, 0) * mm, "end": v(-212.33, 0) * mm});
            skLineSegment(sketch, "E106.0.1", {"start": v(-212.33, 0) * mm, "end": v(-212.33, 44.45) * mm});
            skLineSegment(sketch, "E106.0.2", {"start": v(-212.33, 44.45) * mm, "end": v(-694.93, 44.45) * mm});
            skLineSegment(sketch, "E106.0.3", {"start": v(-694.93, 44.45) * mm, "end": v(-694.93, 0) * mm});
            skSolve(sketch);
        }
        {
            var Q0;
            Q0 = qSketchRegion(id + "F19", true);
            var Q1;
            {var subQ0=sQuery(id+"F14.wireOp",EDGE,"E94.0");Q1=makeQuery(id+"F15.boolean.opBoolean","SPLIT",FACE,{"disambiguationData":[TD([makeQuery(id+"F15.opExtrude","SWEPT_FACE",FACE,{"disambiguationData":[OSD([subQ0]),TDD([makeQuery(id+"F14.imprint","IMPRINT",EDGE,{"disambiguationData":[TD([[makeQuery(id+"F14.imprint","INTERSECT",VERTEX,{"derivedFrom":[subQ0,sQuery(id+"F14.wireOp",EDGE,"E98")]}),-1.0]])],"derivedFrom":subQ0})])]})])],"derivedFrom":makeQuery(id+"F13.opExtrude","SWEPT_FACE",FACE,{"disambiguationData":[OSD([sQuery(id+"F12.wireOp",EDGE,"E91.0.2")])]})});}
            extrude(context, id + "F20", {"entities" : qUnion([Q0]), "operationType" : NewBodyOperationType.ADD, "endBound" : BoundingType.UP_TO_SURFACE, "endBoundEntityFace" : qUnion([Q1]), "depth" : 25.4 * mm});
        }
    });
